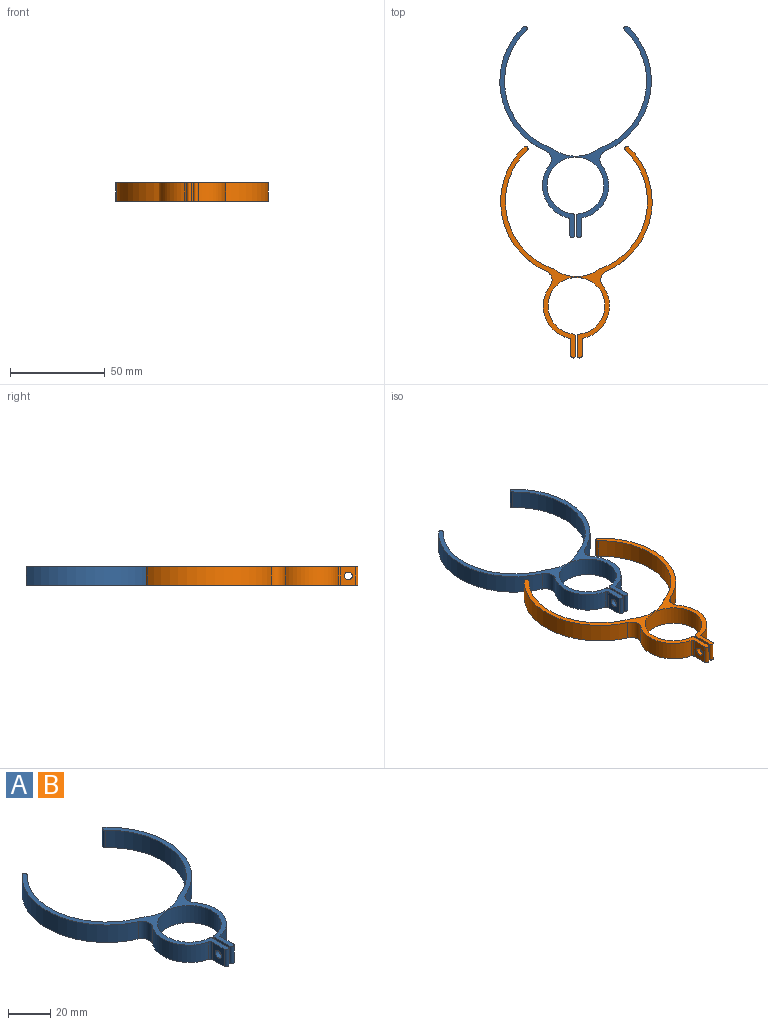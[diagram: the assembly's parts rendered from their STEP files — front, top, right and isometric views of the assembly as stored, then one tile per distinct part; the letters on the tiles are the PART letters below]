
ASSEMBLY  parts=2 mates=1
PART A: 27 faces, bbox 80x111.7x10 mm
  f0: cylinder r=37.5mm len=62.43mm, axis (0,0,-1), area 763.7mm2, adj f3,f4,f16,f20
  f1: cylinder r=40mm len=65.63mm, axis (0,0,-1), area 788.2mm2, adj f3,f4,f19,f21
  f2: cylinder r=37.5mm len=62.43mm, axis (0,0,-1), area 763.7mm2, adj f3,f4,f17,f21
  f3: plane 111.75x80mm, normal (0,0,1), area 737.3mm2, adj f0,f1,f2,f5,f6,f7,f8,f9
  f4: plane 111.75x80mm, normal (0,0,-1), area 737.3mm2, adj f0,f1,f2,f5,f6,f7,f8,f9
  f5: plane 10.09x10mm, normal (1,0,0), area 87mm2, adj f3,f4,f14,f23,f25
  f6: cylinder r=15mm len=30mm, axis (0,0,-1), area 910.1mm2, adj f3,f4,f25,f26
  f7: plane 10.09x10mm, normal (-1,0,0), area 87mm2, adj f3,f4,f13,f24,f26
  f8: plane 10x9mm, normal (1,0,0), area 76.2mm2, adj f3,f4,f9,f13,f24
  f9: cylinder r=17.5mm len=27.89mm, axis (0,0,-1), area 359.2mm2, adj f3,f4,f8,f19
  f10: cylinder r=40mm len=65.63mm, axis (0,0,-1), area 788.2mm2, adj f3,f4,f18,f20
  f11: cylinder r=17.5mm len=27.69mm, axis (0,0,-1), area 349.4mm2, adj f3,f4,f18,f22
  f12: plane 10x7.98mm, normal (-1,0,0), area 66mm2, adj f3,f4,f14,f22,f23
  f13: cylinder r=2.1mm len=4.2mm, axis (-1,0,0), area 33mm2, adj f7,f8
  f14: cylinder r=2.1mm len=4.2mm, axis (-1,0,0), area 33mm2, adj f5,f12
  f15: cylinder r=20mm len=22.81mm, axis (0,0,1), area 242.7mm2, adj f3,f4,f16,f17
  f16: cylinder r=5mm len=10mm, axis (0,0,1), area 13.2mm2, adj f0,f3,f4,f15
  f17: cylinder r=5mm len=10mm, axis (0,0,-1), area 13.2mm2, adj f2,f3,f4,f15
  f18: cylinder r=5mm len=10mm, axis (0,0,1), area 90.9mm2, adj f3,f4,f10,f11
  f19: cylinder r=5mm len=10mm, axis (0,0,1), area 90.9mm2, adj f1,f3,f4,f9
  f20: cylinder r=1.25mm len=10mm, axis (0,0,-1), area 39.3mm2, adj f0,f3,f4,f10
  f21: cylinder r=1.25mm len=10mm, axis (0,0,1), area 39.3mm2, adj f1,f2,f3,f4
  f22: cylinder r=1.25mm len=10mm, axis (0,0,-1), area 16.8mm2, adj f3,f4,f11,f12
  f23: cylinder r=1.25mm len=10mm, axis (0,0,-1), area 39.3mm2, adj f3,f4,f5,f12
  f24: cylinder r=1.25mm len=10mm, axis (0,0,1), area 39.3mm2, adj f3,f4,f7,f8
  f25: cylinder r=1.25mm len=10mm, axis (0,0,-1), area 18.3mm2, adj f3,f4,f5,f6
  f26: cylinder r=1.25mm len=10mm, axis (0,0,-1), area 18.3mm2, adj f3,f4,f6,f7
PART B: same geometry as A
PLACE A t=(-21.04,41.02,25.79)mm
PLACE B t=(-20.61,-22.52,25.79)mm
MATE planar A.f3 <-> B.f3  axis (0,0,1) through (-33.61,44.44,35.79)mm
